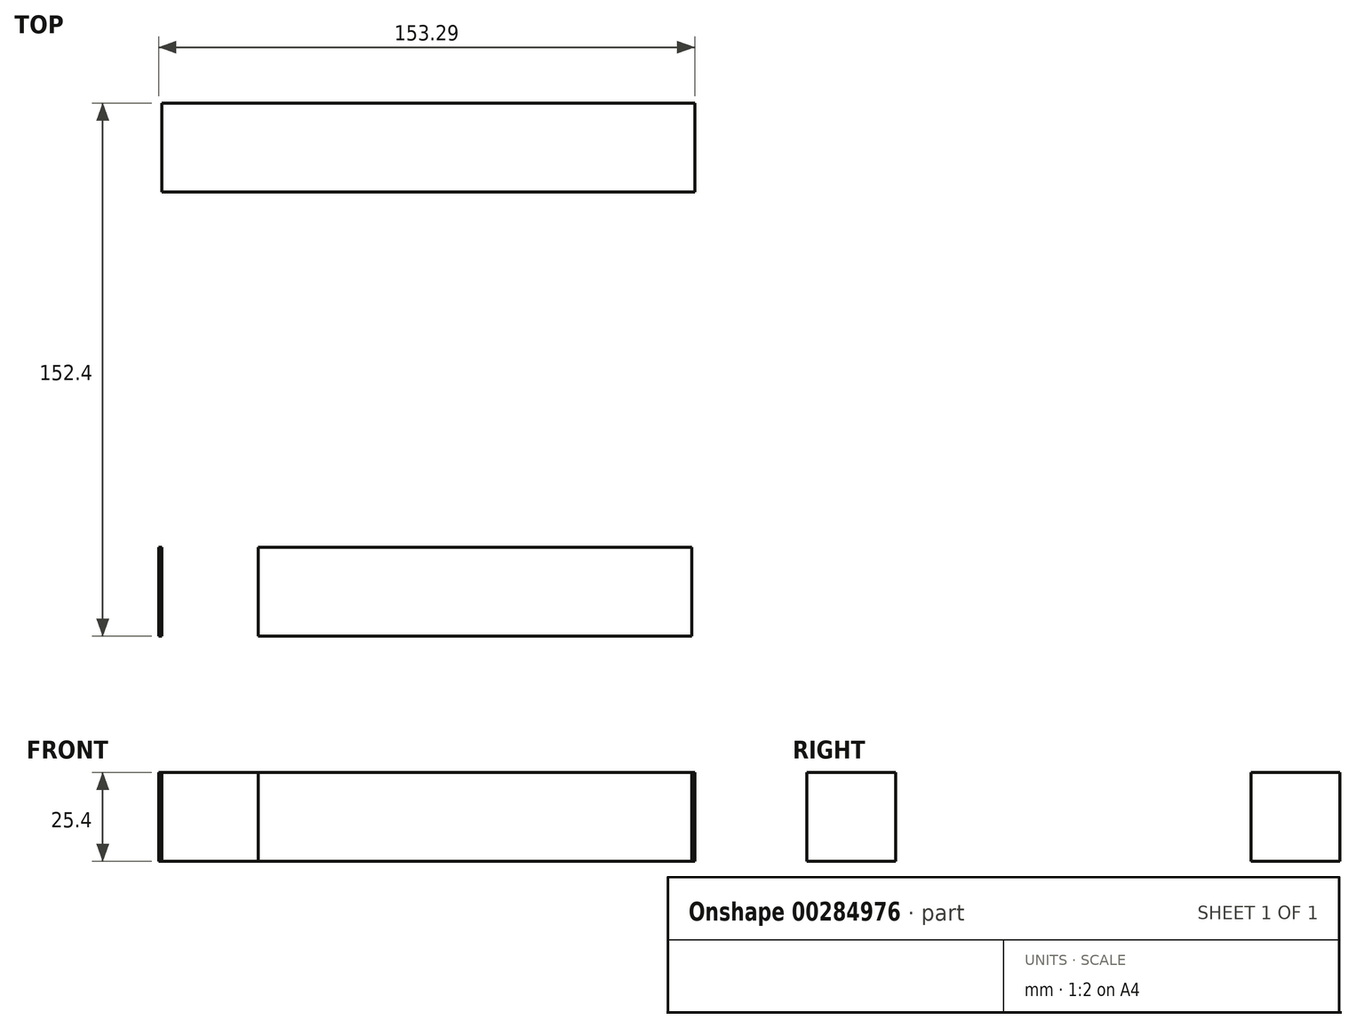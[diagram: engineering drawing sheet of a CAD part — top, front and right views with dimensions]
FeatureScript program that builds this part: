
annotation { "Feature Type Name" : "Feature", "Feature Type Description" : "" }
export const myFeature = defineFeature(function(context is Context, id is Id, definition is map)
    precondition{}
    {
        {
            var Q0;
            Q0=qCreatedBy(makeId("Top.planeOp"),FACE);
            var sketch = newSketch(context, id + "F0", { "sketchPlane" : qUnion([Q0])});
            skLineSegment(sketch, "E0.bottom", {"start": v(-76.5, 76.21) * mm, "end": v(75.9, 76.21) * mm});
            skLineSegment(sketch, "E0.top", {"start": v(-76.5, 50.81) * mm, "end": v(75.9, 50.81) * mm});
            skLineSegment(sketch, "E0.left", {"start": v(-76.5, 76.21) * mm, "end": v(-76.5, 50.81) * mm});
            skLineSegment(sketch, "E0.right", {"start": v(75.9, 76.21) * mm, "end": v(75.9, 50.81) * mm});
            skLineSegment(sketch, "E1.bottom", {"start": v(-77.38, -76.19) * mm, "end": v(75.02, -76.19) * mm});
            skLineSegment(sketch, "E1.top", {"start": v(-77.38, -50.79) * mm, "end": v(75.02, -50.79) * mm});
            skLineSegment(sketch, "E1.left", {"start": v(-77.38, -76.19) * mm, "end": v(-77.38, -50.79) * mm});
            skLineSegment(sketch, "E1.right", {"start": v(75.02, -76.19) * mm, "end": v(75.02, -50.79) * mm});
            skLineSegment(sketch, "E2.bottom", {"start": v(-76.5, 76.21) * mm, "end": v(-48.86, 76.21) * mm});
            skLineSegment(sketch, "E2.top", {"start": v(-76.5, -76.19) * mm, "end": v(-48.86, -76.19) * mm});
            skLineSegment(sketch, "E2.left", {"start": v(-76.5, 76.21) * mm, "end": v(-76.5, -76.19) * mm});
            skLineSegment(sketch, "E2.right", {"start": v(-48.86, 76.21) * mm, "end": v(-48.86, -76.19) * mm});
            skSolve(sketch);
        }
        {
            var Q0;
            {var subQ0=sQuery(id+"F0.wireOp",EDGE,"E0.bottom");Q0=makeQuery(id+"F0.imprint","IMPRINT",FACE,{"disambiguationData":[TD([[makeQuery(id+"F0.imprint","IMPRINT",EDGE,{"derivedFrom":subQ0}),-1.0]])]});}
            var Q1;
            {var subQ0=sQuery(id+"F0.wireOp",EDGE,"E1.left");Q1=makeQuery(id+"F0.imprint","IMPRINT",FACE,{"disambiguationData":[TD([[makeQuery(id+"F0.imprint","IMPRINT",EDGE,{"derivedFrom":subQ0}),-1.0]])]});}
            var Q2;
            {var subQ0=sQuery(id+"F0.wireOp",EDGE,"E1.right");Q2=makeQuery(id+"F0.imprint","IMPRINT",FACE,{"disambiguationData":[TD([[makeQuery(id+"F0.imprint","IMPRINT",EDGE,{"derivedFrom":subQ0}),1.0]])]});}
            var Q3;
            {var subQ5=sQuery(id+"F0.wireOp",EDGE,"E2.bottom");Q3=makeQuery(id+"F0.imprint","IMPRINT",FACE,{"disambiguationData":[TD([[makeQuery(id+"F0.imprint","IMPRINT",EDGE,{"derivedFrom":subQ5}),-1.0]])]});}
            var Q4;
            {var subQ5=sQuery(id+"F0.wireOp",EDGE,"E2.top");Q4=makeQuery(id+"F0.imprint","IMPRINT",FACE,{"disambiguationData":[TD([[makeQuery(id+"F0.imprint","IMPRINT",EDGE,{"derivedFrom":subQ5}),1.0]])]});}
            extrude(context, id + "F1", {"entities" : qUnion([Q0, Q1, Q2, Q3, Q4]), "endBound" : BoundingType.SYMMETRIC, "depth" : 25.4 * mm});
        }
    });
